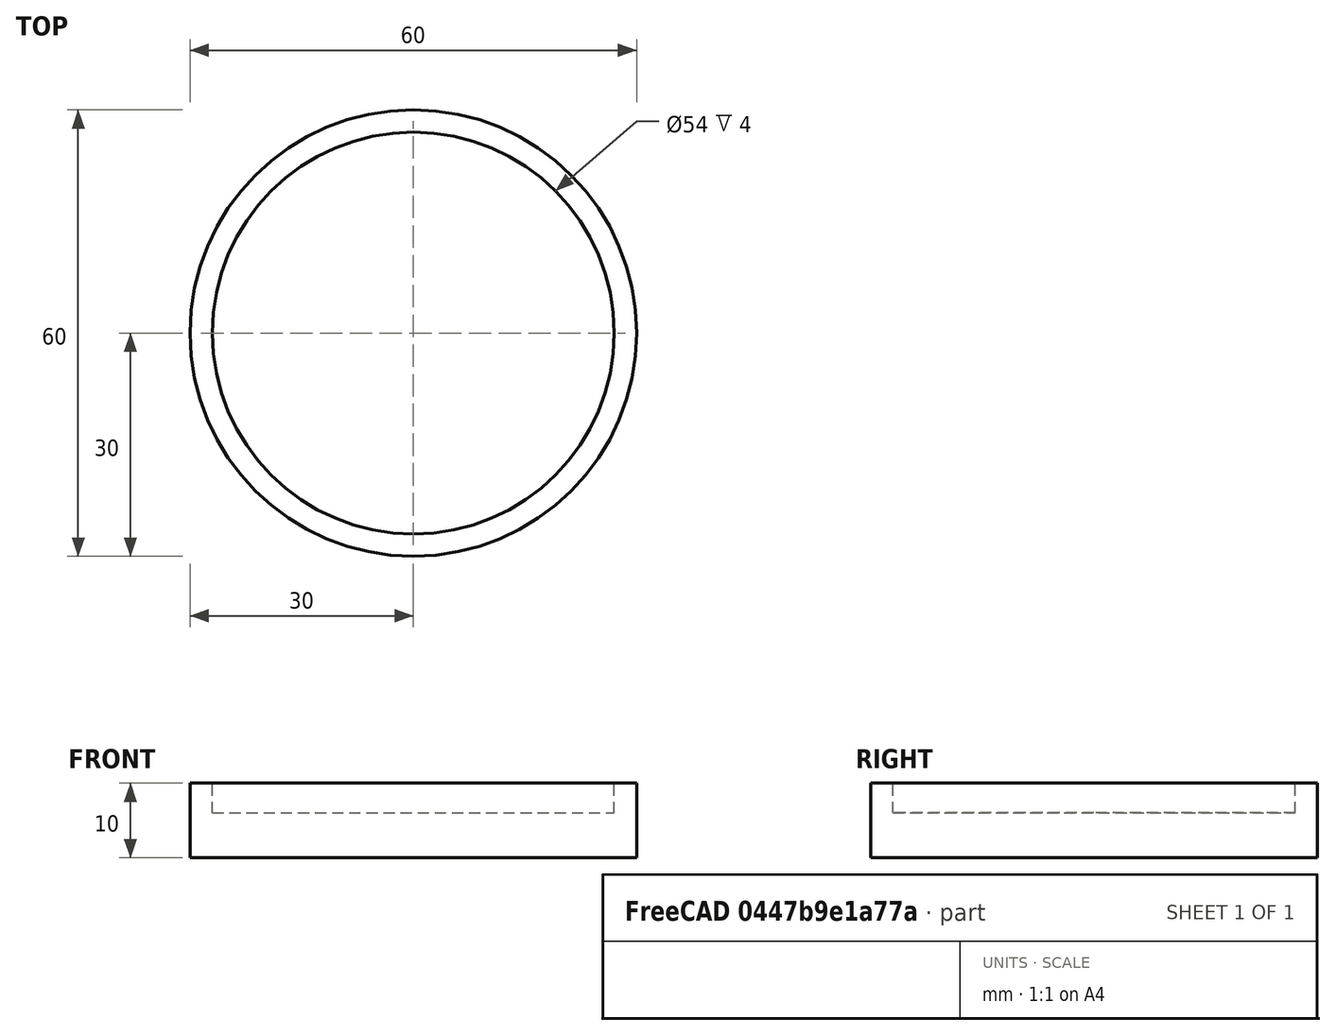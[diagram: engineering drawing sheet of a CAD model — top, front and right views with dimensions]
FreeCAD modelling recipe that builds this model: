
FCSTD DOCUMENT  (FreeCAD 0.18.4R)
Label: gauge-top
License: All rights reserved
LicenseURL: http://en.wikipedia.org/wiki/All_rights_reserved
objects: Sketcher::SketchObject×1, PartDesign::Revolution×1, PartDesign::Body×1
note: 4 computed .brp shape members not serialized (recipe doc carries the construction recipe); baked Part::Feature solids carry a one-line shape summary decoded from their .brp

FEATURE [Sketcher::SketchObject] Sketch
  MapMode = 5
  Placement = pos=(0,0,0) rot=(1,0,0;1.5708rad)
  Support = -> [XZ_Plane]
  sketch-geometry (6):
    g0: LineSegment StartX=0 StartY=6 StartZ=0 EndX=-27 EndY=6 EndZ=0
    g1: LineSegment StartX=-27 StartY=6 StartZ=0 EndX=-27 EndY=10 EndZ=0
    g2: LineSegment StartX=-27 StartY=10 StartZ=0 EndX=-30 EndY=10 EndZ=0
    g3: LineSegment StartX=-30 StartY=10 StartZ=0 EndX=-30 EndY=0 EndZ=0
    g4: LineSegment StartX=-30 StartY=0 StartZ=0 EndX=0 EndY=0 EndZ=0
    g5: LineSegment StartX=0 StartY=0 StartZ=0 EndX=0 EndY=6 EndZ=0
  constraints (17):
    c: PointOnObject(g0,g-2)
    c: Horizontal(g0)
    c: Coincident(g0,g1)
    c: Vertical(g1)
    c: Coincident(g1,g2)
    c: Horizontal(g2)
    c: Coincident(g2,g3)
    c: PointOnObject(g3,g-1)
    c: Vertical(g3)
    c: Coincident(g3,g4)
    c: Coincident(g4,g-1)
    c: Coincident(g4,g5)
    c: Coincident(g5,g0)
    c: DistanceY(g3,g3) = 10
    c: DistanceX(g2,g2) = 3
    c: DistanceY(g1,g1) = 4
    c: DistanceX(g4,g4) = 30
FEATURE [PartDesign::Revolution] Revolution
  Angle = 360
  Axis = (0,2e-16,1)
  Base = (0,0,0)
  Placement = pos=(0,0,0) rot=(1,0,0;1.5708rad)
  Profile = -> Sketch
  ReferenceAxis = -> Sketch [V_Axis]
FEATURE [PartDesign::Body] Body
  Group = -> [Sketch,Revolution]
  Origin = -> Origin
  Tip = -> Revolution
